# Revit family: equip-sink-elkay-lav-wall-elv1817
name_source: partatom
category: Plumbing Fixtures
units: mm (PartAtom-declared; Revit-internal decimal feet)

## family parameters
Cut with Voids When Loaded = No
Host = Face
Part Type = Normal
Room Calculation Point = No
Round Connector Dimension = Use Diameter
Shared = No

## types (2) — shared parameters
Assembly Code = D2010410
Bowl Depth = 0' - 5 3/4"
Bubbler Material = Metal - Steel - Stainless - Chrome
CW Flow Rate = 2 GPM
Cost = 1 $
Default Elevation = 2' - 7 1/2"
Description = Wash-Up Lavatory Sinks
Drain Material = Metal - Steel - Stainless - Chrome
Faucet Hole One = Yes
Faucet Hole One Top = 0' - 0 1/4"
Faucet Hole Three = Yes
Faucet Hole Three Top = 0' - 0 1/4"
Faucet Hole Two = Yes
Faucet Hole Two Top = 0' - 0 1/4"
Faucet Material = Metal - Steel - Stainless - Chrome
HW Flow Rate = 2 GPM
Keynote = D2010410
Manufacturer = Elkay Manufacturing
MasterFormat Number = 22.42.16.16
MasterFormat Title = Commercial Sinks
Model = ELV17183
Nominal Dia = 0' - 0 1/2"
Nominal Radius = 0' - 0 1/4"
OmniClass Code = 23.45.05.14.14.27
OmniClass Title = Service Sinks
OverFlow = No
San Conn Extr Visibility = No
Sanitary Flow Rate = 10 GPM
Sanitary Nominal Dia = 0' - 1 1/2"
Sanitary Nominal Radius = 0' - 0 3/4"
Sink Length = 1' - 7 5/8"
Sink Material = Metal - Steel - Stainless - Chrome
Sink Part = ELV17183
Sink Width = 1' - 6 3/4"
Specification Sheet URL = http://www.elkayusa.com
Stem Material = Metal - Steel
URL = www.elkayusa.com
Vent Connection = Yes
zero-valued in all types: CWFU, HWFU, WFU

## per-type parameters (varying)
| type | Faucet Hole Dia | Faucet Hole One to CL | Hole One to Three | Hole One to Two | Hole Radius |
| ELV17183 | 0' - 1 1/2" | 0' - 4" | 0' - 8" | 0' - 4" | 0' - 0 3/4" |
| ELV1817CS3 | 0' - 1 1/4" | 0' - 2" | 0' - 4" | 0' - 2" | 0' - 0 5/8" |

## geometry (parser evidence)
native form markers: Sweep x9
no freeform markers — native parametric forms only
